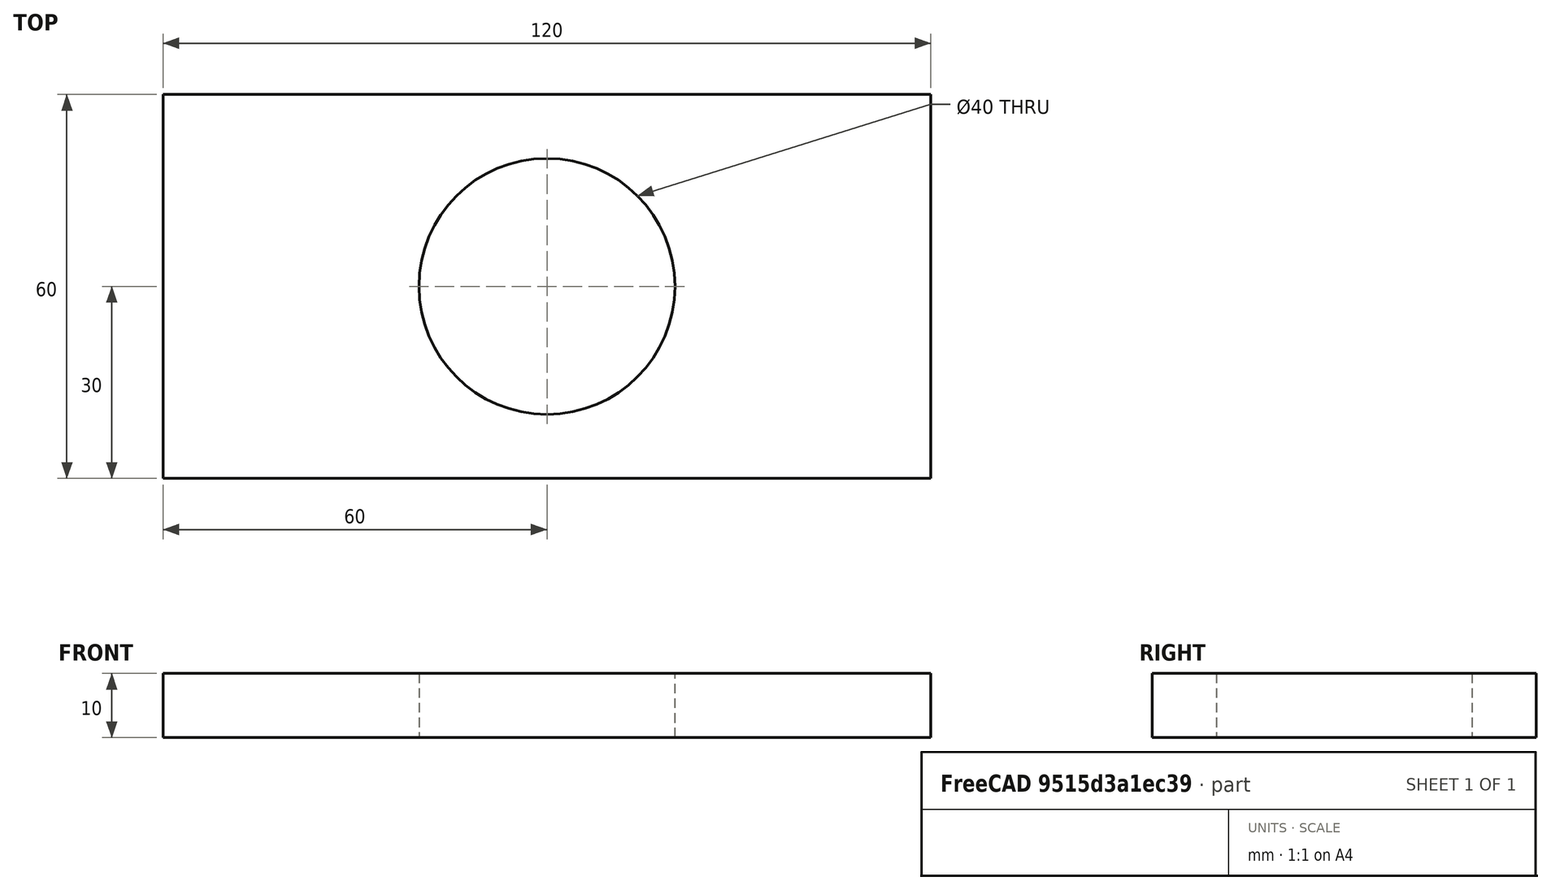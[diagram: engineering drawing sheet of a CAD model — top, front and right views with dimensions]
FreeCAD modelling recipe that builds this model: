
FCSTD DOCUMENT  (FreeCAD 0.16R6706 (Git))
Label: Placa_furo
License: All rights reserved
LicenseURL: http://en.wikipedia.org/wiki/All_rights_reserved
objects: Sketcher::SketchObject×1, PartDesign::Pad×1
note: 3 computed .brp shape members not serialized (recipe doc carries the construction recipe); baked Part::Feature solids carry a one-line shape summary decoded from their .brp

FEATURE [Sketcher::SketchObject] Sketch
  sketch-geometry (5):
    g0: Circle CenterX=0 CenterY=0 CenterZ=0 NormalX=0 NormalY=0 NormalZ=1 Radius=20
    g1: LineSegment StartX=-60 StartY=30 StartZ=0 EndX=60 EndY=30 EndZ=0
    g2: LineSegment StartX=60 StartY=30 StartZ=0 EndX=60 EndY=-30 EndZ=0
    g3: LineSegment StartX=60 StartY=-30 StartZ=0 EndX=-60 EndY=-30 EndZ=0
    g4: LineSegment StartX=-60 StartY=-30 StartZ=0 EndX=-60 EndY=30 EndZ=0
  constraints (14):
    c: Coincident(g0,g-1)
    c: Coincident(g1,g2)
    c: Coincident(g2,g3)
    c: Coincident(g3,g4)
    c: Coincident(g4,g1)
    c: Horizontal(g1)
    c: Horizontal(g3)
    c: Vertical(g2)
    c: Vertical(g4)
    c: Symmetric(g1,g1,g-2)
    c: Symmetric(g1,g2,g-1)
    c: DistanceX(g1,g1) = 120
    c: DistanceY(g2,g2) = 60
    c: Radius(g0) = 20
FEATURE [PartDesign::Pad] Pad
  Length = 10
  Length2 = 100
  Sketch = -> Sketch
  Type = 0
